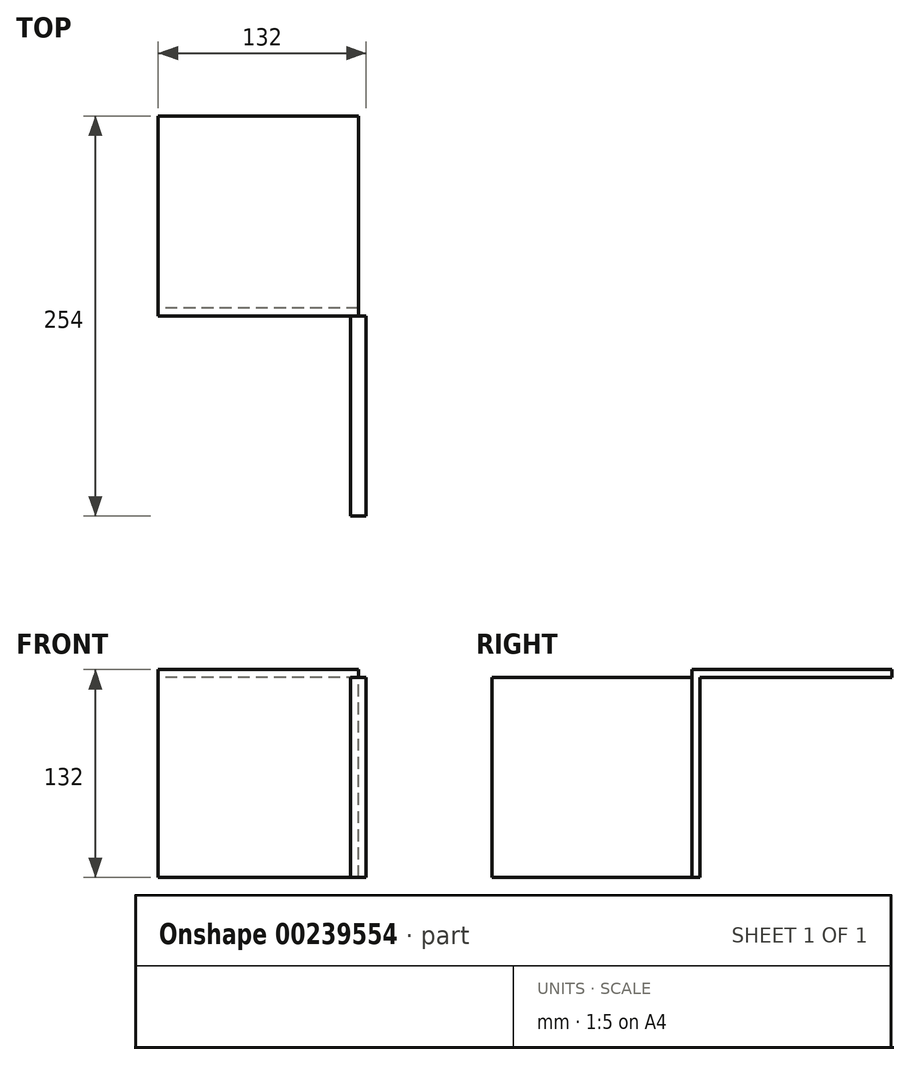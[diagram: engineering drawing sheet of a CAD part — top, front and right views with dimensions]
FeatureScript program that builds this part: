
annotation { "Feature Type Name" : "Feature", "Feature Type Description" : "" }
export const myFeature = defineFeature(function(context is Context, id is Id, definition is map)
    precondition{}
    {
        {
            assignVariable(context, id + "F0", {"name" : "L", "anyValue" : 5});
        }
        {
            var Q0;
            Q0=qCreatedBy(makeId("Right.planeOp"),FACE);
            var sketch = newSketch(context, id + "F1", { "sketchPlane" : qUnion([Q0])});
            skLineSegment(sketch, "E0.bottom", {"start": v(63.5, 63.5) * mm, "end": v(-63.5, 63.5) * mm});
            skLineSegment(sketch, "E0.top", {"start": v(63.5, -63.5) * mm, "end": v(-63.5, -63.5) * mm});
            skLineSegment(sketch, "E0.left", {"start": v(63.5, 63.5) * mm, "end": v(63.5, -63.5) * mm});
            skLineSegment(sketch, "E0.right", {"start": v(-63.5, 63.5) * mm, "end": v(-63.5, -63.5) * mm});
            skPoint(sketch, "E0.middle", {"position": v(0, 0) * mm});
            skSolve(sketch);
        }
        {
            var Q0;
            Q0=qSketchRegion(id+"F1",true);
            extrude(context, id + "F2", {"entities" : qUnion([Q0]), "endBound" : BoundingType.SYMMETRIC, "depth" : (getVariable(context, 'L') * 2) * mm});
        }
        {
            var Q0;
            Q0=makeQuery(id+"F2.opExtrude","SWEPT_FACE",FACE,{"disambiguationData":[OSD([sQuery(id+"F1.wireOp",EDGE,"E0.left")])]});
            var sketch = newSketch(context, id + "F3", { "sketchPlane" : qUnion([Q0])});
            skLineSegment(sketch, "E1.bottom", {"start": v(0, -63.5) * mm, "end": v(127, -63.5) * mm});
            skLineSegment(sketch, "E1.top", {"start": v(0, 63.5) * mm, "end": v(127, 63.5) * mm});
            skLineSegment(sketch, "E1.left", {"start": v(0, -63.5) * mm, "end": v(0, 63.5) * mm});
            skLineSegment(sketch, "E1.right", {"start": v(127, -63.5) * mm, "end": v(127, 63.5) * mm});
            skSolve(sketch);
        }
        {
            var Q0;
            Q0=qSketchRegion(id+"F3",true);
            extrude(context, id + "F4", {"entities" : qUnion([Q0]), "operationType" : NewBodyOperationType.ADD, "depth" : (getVariable(context, 'L')) * mm});
        }
        {
            var Q0;
            Q0=makeQuery(id+"F4.boolean.opBoolean","MERGE",FACE,{"derivedFrom":[makeQuery(id+"F2.opExtrude","SWEPT_FACE",FACE,{"disambiguationData":[OSD([sQuery(id+"F1.wireOp",EDGE,"E0.bottom")])]}),makeQuery(id+"F4.opExtrude","SWEPT_FACE",FACE,{"disambiguationData":[OSD([sQuery(id+"F3.wireOp",EDGE,"E1.top")])]})]});
            var sketch = newSketch(context, id + "F5", { "sketchPlane" : qUnion([Q0])});
            skLineSegment(sketch, "E2.bottom", {"start": v(0, 63.5) * mm, "end": v(-127, 63.5) * mm});
            skLineSegment(sketch, "E2.top", {"start": v(0, 190.5) * mm, "end": v(-127, 190.5) * mm});
            skLineSegment(sketch, "E2.left", {"start": v(0, 63.5) * mm, "end": v(0, 190.5) * mm});
            skLineSegment(sketch, "E2.right", {"start": v(-127, 63.5) * mm, "end": v(-127, 190.5) * mm});
            skSolve(sketch);
        }
        {
            var Q0;
            Q0=qSketchRegion(id+"F5",true);
            extrude(context, id + "F6", {"entities" : qUnion([Q0]), "operationType" : NewBodyOperationType.ADD, "depth" : (getVariable(context, 'L')) * mm});
        }
    });
